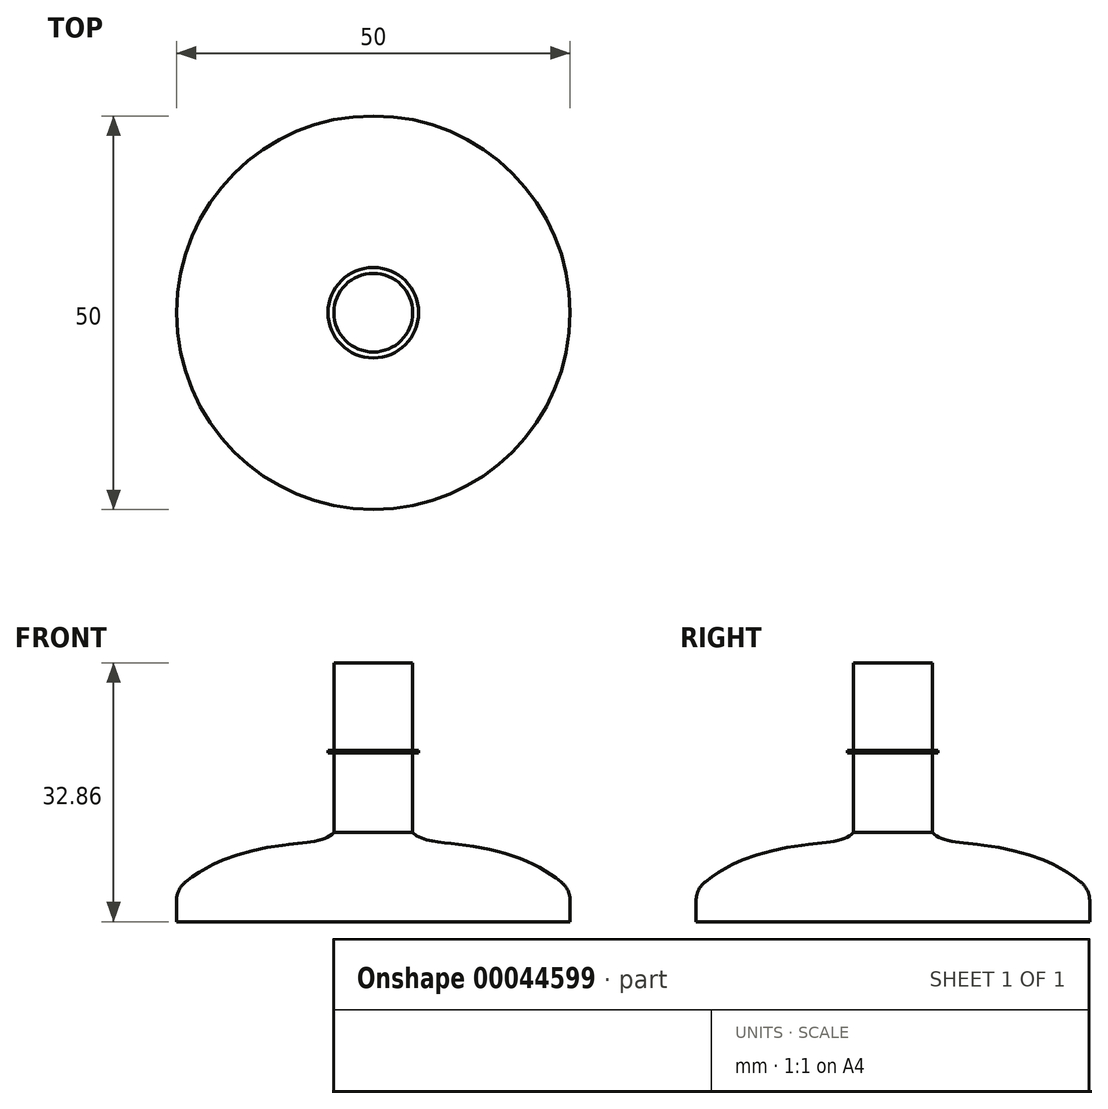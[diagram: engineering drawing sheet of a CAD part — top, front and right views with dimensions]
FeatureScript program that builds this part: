
annotation { "Feature Type Name" : "Feature", "Feature Type Description" : "" }
export const myFeature = defineFeature(function(context is Context, id is Id, definition is map)
    precondition{}
    {
        {
            var Q0;
            Q0=qCreatedBy(makeId("Front.planeOp"),FACE);
            var sketch = newSketch(context, id + "F0", { "sketchPlane" : qUnion([Q0])});
            skLineSegment(sketch, "E0", {"start": v(0, 15.46) * mm, "end": v(0, -17.4) * mm});
            skLineSegment(sketch, "E1", {"start": v(0, -17.4) * mm, "end": v(-25, -17.4) * mm});
            skLineSegment(sketch, "E2", {"start": v(-25, -17.4) * mm, "end": v(-25, -14.73) * mm});
            skFitSpline(sketch, "E3", {"points": [v(-25, -13.27) * mm, v(-19.34, -9.65) * mm, v(-10, -7.49) * mm, v(-5, -6.06) * mm], "startDerivative": vector(15.08, 12.05) * mm, "endDerivative": vector(11.98, 11.9) * mm});
            skLineSegment(sketch, "E4", {"start": v(-5, -6.06) * mm, "end": v(-5, 4.02) * mm});
            skLineSegment(sketch, "E5", {"start": v(-5, 15.46) * mm, "end": v(0, 15.46) * mm});
            skArc(sketch, "E6.filletArc", {"start": v(-23.82, -12.34) * mm, "mid": v(-24.69, -13.4) * mm, "end": v(-25, -14.73) * mm});
            skLineSegment(sketch, "E7.bottom", {"start": v(-5.75, 4.36) * mm, "end": v(-5, 4.36) * mm});
            skLineSegment(sketch, "E7.top", {"start": v(-5.75, 4.02) * mm, "end": v(-5, 4.02) * mm});
            skLineSegment(sketch, "E7.left", {"start": v(-5.75, 4.36) * mm, "end": v(-5.75, 4.02) * mm});
            skLineSegment(sketch, "E8.trimOffspring", {"start": v(-5, 4.36) * mm, "end": v(-5, 15.46) * mm});
            skSolve(sketch);
        }
        {
            var Q0;
            Q0=makeQuery(id+"F0.imprint","IMPRINT",FACE,{"disambiguationData":[TD([[makeQuery(id+"F0.imprint","IMPRINT",EDGE,{"derivedFrom":sQuery(id+"F0.wireOp",EDGE,"E0")}),-1.0]])]});
            var Q1;
            Q1=sQuery(id+"F0.wireOp",EDGE,"E0");
            revolve(context, id + "F1", {"entities" : qUnion([Q0]), "axis" : qUnion([Q1]), "revolveType" : RevolveType.FULL});
        }
    });
